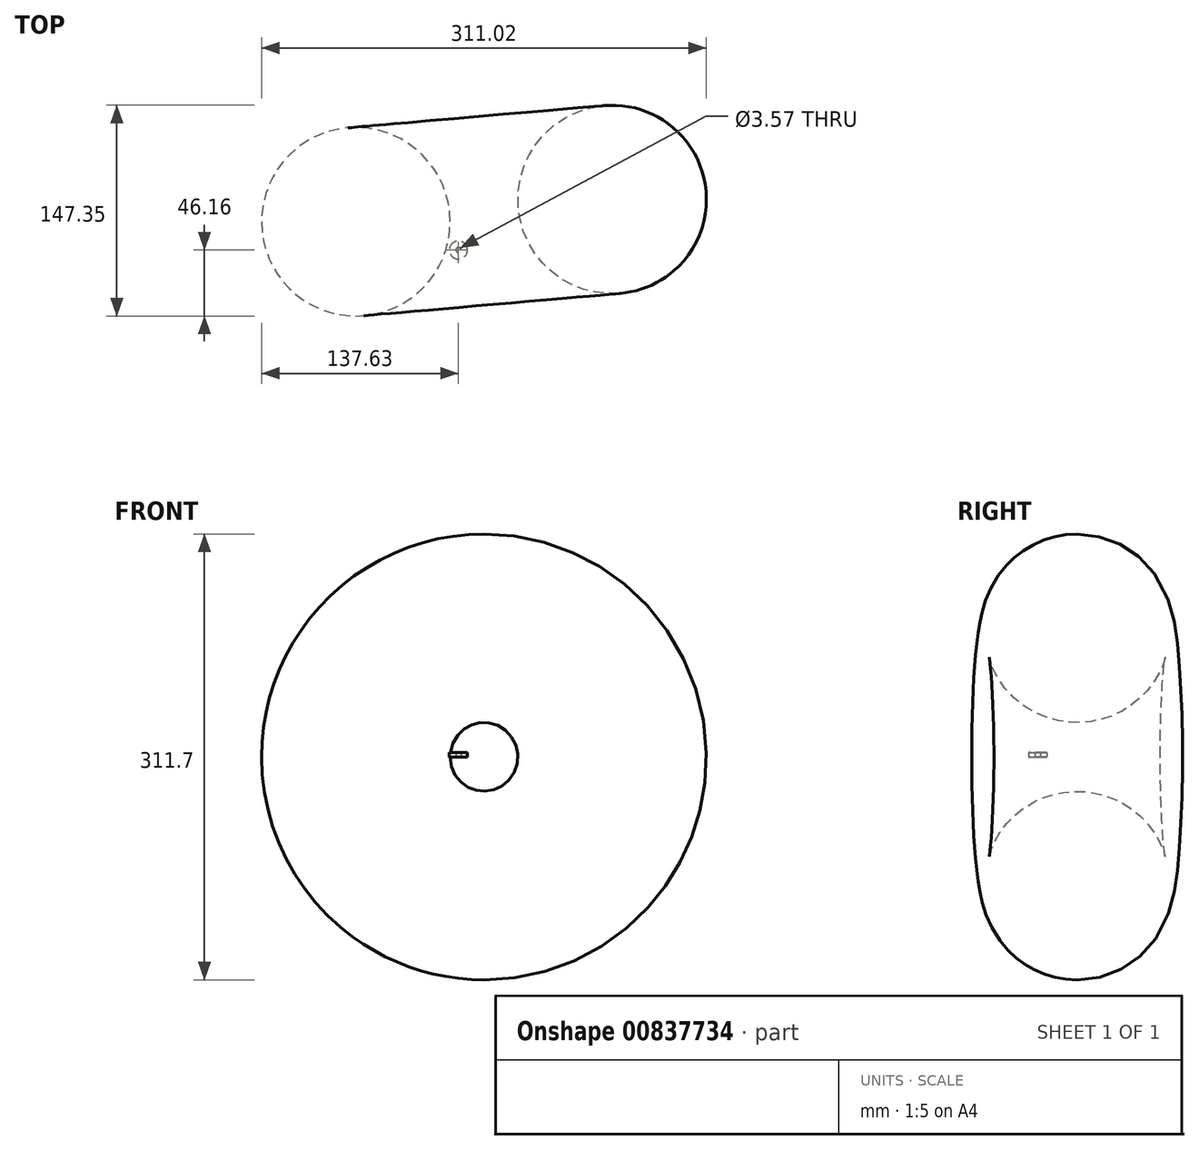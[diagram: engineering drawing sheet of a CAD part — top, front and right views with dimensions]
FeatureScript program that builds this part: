
annotation { "Feature Type Name" : "Feature", "Feature Type Description" : "" }
export const myFeature = defineFeature(function(context is Context, id is Id, definition is map)
    precondition{}
    {
        {
            var Q0;
            Q0=qCreatedBy(makeId("Top.planeOp"),FACE);
            var sketch = newSketch(context, id + "F0", { "sketchPlane" : qUnion([Q0])});
            skCircle(sketch, "E0", {"center": v(0, 0) * mm, "radius": 6.35 * mm});
            skCircle(sketch, "E1", {"center": v(0, 0) * mm, "radius": 1.79 * mm});
            skSolve(sketch);
        }
        {
            var Q0;
            Q0=makeQuery(id+"F0.imprint","IMPRINT",FACE,{"disambiguationData":[TD([[makeQuery(id+"F0.imprint","IMPRINT",EDGE,{"derivedFrom":sQuery(id+"F0.wireOp",EDGE,"E0")}),1.0]])]});
            extrude(context, id + "F1", {"entities" : qUnion([Q0]), "depth" : 3.17 * mm, "offsetDistance" : 25.4 * mm});
        }
        {
            var Q0;
            Q0=qCreatedBy(makeId("Top.planeOp"),FACE);
            var sketch = newSketch(context, id + "F2", { "sketchPlane" : qUnion([Q0])});
            skCircle(sketch, "E2", {"center": v(-71.73, 19.74) * mm, "radius": 65.9 * mm});
            skLineSegment(sketch, "E3", {"start": v(14.69, 64.34) * mm, "end": v(18.2, 23.81) * mm});
            skSolve(sketch);
        }
        {
            var Q0;
            Q0=makeQuery(id+"F2.imprint","IMPRINT",FACE,{"disambiguationData":[TD([[makeQuery(id+"F2.imprint","IMPRINT",EDGE,{"derivedFrom":sQuery(id+"F2.wireOp",EDGE,"E2")}),1.0]])]});
            var Q1;
            Q1=sQuery(id+"F2.wireOp",EDGE,"E3");
            revolve(context, id + "F3", {"surfaceOperationType" : NewSurfaceOperationType.NEW, "entities" : qUnion([Q0]), "axis" : qUnion([Q1]), "revolveType" : RevolveType.FULL});
        }
    });
